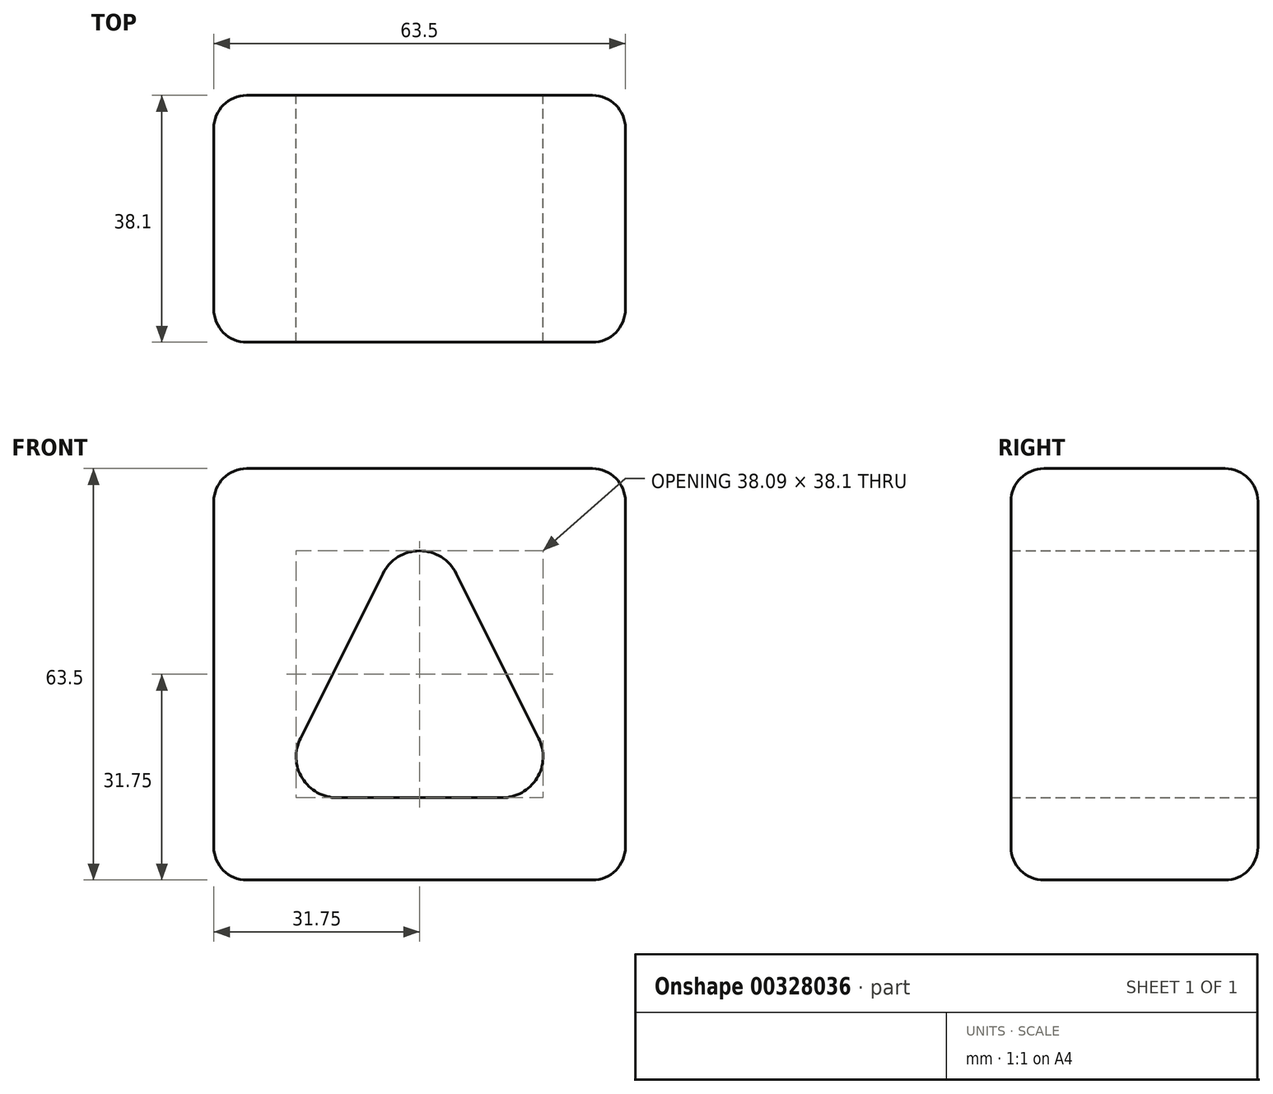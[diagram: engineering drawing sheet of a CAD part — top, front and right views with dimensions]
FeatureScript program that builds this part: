
annotation { "Feature Type Name" : "Feature", "Feature Type Description" : "" }
export const myFeature = defineFeature(function(context is Context, id is Id, definition is map)
    precondition{}
    {
        {
            var Q0;
            Q0=qCreatedBy(makeId("Front.planeOp"),FACE);
            var sketch = newSketch(context, id + "F0", { "sketchPlane" : qUnion([Q0])});
            skLineSegment(sketch, "E0", {"start": v(0, 0) * mm, "end": v(63.5, 0) * mm});
            skLineSegment(sketch, "E1", {"start": v(63.5, 0) * mm, "end": v(63.5, 63.5) * mm});
            skLineSegment(sketch, "E2", {"start": v(63.5, 63.5) * mm, "end": v(0, 63.5) * mm});
            skLineSegment(sketch, "E3", {"start": v(0, 63.5) * mm, "end": v(0, 0) * mm});
            skArc(sketch, "E4", {"start": v(13.37, 21.89) * mm, "mid": v(13.65, 15.71) * mm, "end": v(19.05, 12.7) * mm});
            skArc(sketch, "E5", {"start": v(37.43, 47.29) * mm, "mid": v(31.75, 50.8) * mm, "end": v(26.07, 47.29) * mm});
            skArc(sketch, "E6", {"start": v(44.45, 12.7) * mm, "mid": v(49.85, 15.71) * mm, "end": v(50.13, 21.89) * mm});
            skLineSegment(sketch, "E7", {"start": v(37.43, 47.29) * mm, "end": v(50.13, 21.89) * mm});
            skLineSegment(sketch, "E8", {"start": v(44.45, 12.7) * mm, "end": v(19.05, 12.7) * mm});
            skLineSegment(sketch, "E9", {"start": v(26.07, 47.29) * mm, "end": v(13.37, 21.89) * mm});
            skSolve(sketch);
        }
        {
            var Q0;
            Q0=makeQuery(id+"F0.imprint","IMPRINT",FACE,{"disambiguationData":[TD([[makeQuery(id+"F0.imprint","IMPRINT",EDGE,{"derivedFrom":sQuery(id+"F0.wireOp",EDGE,"E0")}),1.0]])]});
            extrude(context, id + "F1", {"entities" : qUnion([Q0]), "depth" : 38.1 * mm});
        }
        {
            var Q0;
            Q0=makeQuery(id+"F1.opExtrude","CAP_EDGE",EDGE,{"disambiguationData":[OSD([sQuery(id+"F0.wireOp",EDGE,"E2")])],"isStart":false});
            var Q1;
            Q1=makeQuery(id+"F1.opExtrude","SWEPT_EDGE",EDGE,{"disambiguationData":[OSD([sQuery(id+"F0.wireOp",EDGE,"E1"),sQuery(id+"F0.wireOp",EDGE,"E2")])]});
            var Q2;
            Q2=makeQuery(id+"F1.opExtrude","CAP_EDGE",EDGE,{"disambiguationData":[OSD([sQuery(id+"F0.wireOp",EDGE,"E2")])],"isStart":true});
            var Q3;
            Q3=makeQuery(id+"F1.opExtrude","SWEPT_EDGE",EDGE,{"disambiguationData":[OSD([sQuery(id+"F0.wireOp",EDGE,"E2"),sQuery(id+"F0.wireOp",EDGE,"E3")])]});
            var Q4;
            Q4=makeQuery(id+"F1.opExtrude","CAP_EDGE",EDGE,{"disambiguationData":[OSD([sQuery(id+"F0.wireOp",EDGE,"E3")])],"isStart":true});
            var Q5;
            Q5=makeQuery(id+"F1.opExtrude","CAP_EDGE",EDGE,{"disambiguationData":[OSD([sQuery(id+"F0.wireOp",EDGE,"E3")])],"isStart":false});
            var Q6;
            Q6=makeQuery(id+"F1.opExtrude","SWEPT_EDGE",EDGE,{"disambiguationData":[OSD([sQuery(id+"F0.wireOp",EDGE,"E0"),sQuery(id+"F0.wireOp",EDGE,"E3")])]});
            var Q7;
            Q7=makeQuery(id+"F1.opExtrude","CAP_EDGE",EDGE,{"disambiguationData":[OSD([sQuery(id+"F0.wireOp",EDGE,"E0")])],"isStart":true});
            var Q8;
            Q8=makeQuery(id+"F1.opExtrude","CAP_EDGE",EDGE,{"disambiguationData":[OSD([sQuery(id+"F0.wireOp",EDGE,"E0")])],"isStart":false});
            var Q9;
            Q9=makeQuery(id+"F1.opExtrude","SWEPT_EDGE",EDGE,{"disambiguationData":[OSD([sQuery(id+"F0.wireOp",EDGE,"E0"),sQuery(id+"F0.wireOp",EDGE,"E1")])]});
            var Q10;
            Q10=makeQuery(id+"F1.opExtrude","CAP_EDGE",EDGE,{"disambiguationData":[OSD([sQuery(id+"F0.wireOp",EDGE,"E1")])],"isStart":true});
            var Q11;
            Q11=makeQuery(id+"F1.opExtrude","CAP_EDGE",EDGE,{"disambiguationData":[OSD([sQuery(id+"F0.wireOp",EDGE,"E1")])],"isStart":false});
            fillet(context, id + "F2", {"entities" : qUnion([Q0, Q1, Q2, Q3, Q4, Q5, Q6, Q7, Q8, Q9, Q10, Q11]), "radius" : 5.08 * mm, "tangentPropagation" : true, "allowEdgeOverflow" : false});
        }
    });
